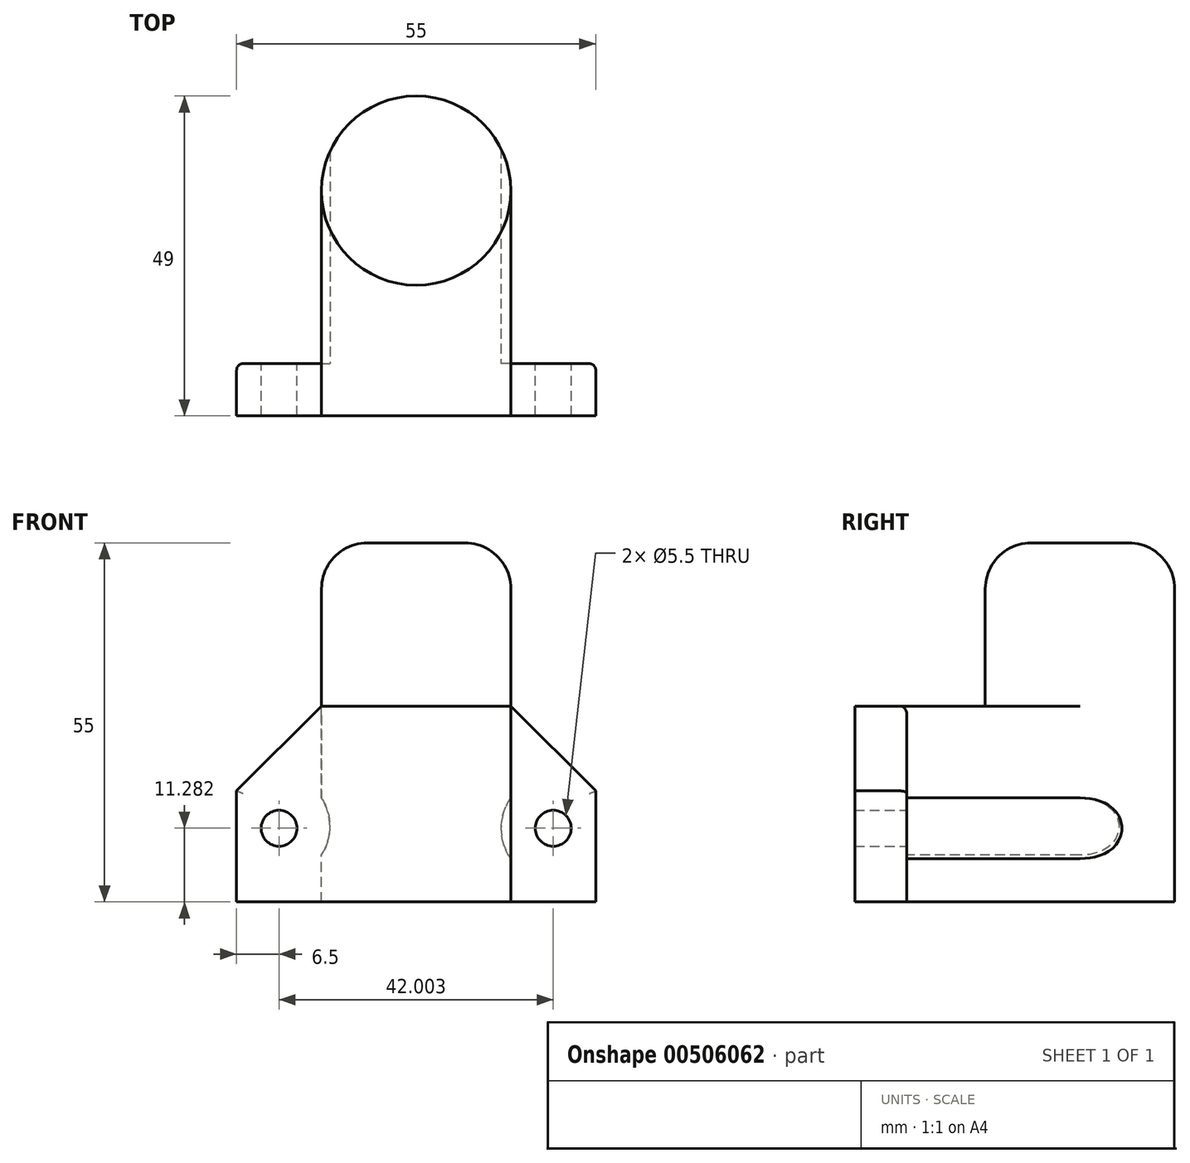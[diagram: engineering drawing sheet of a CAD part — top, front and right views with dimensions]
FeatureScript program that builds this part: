
annotation { "Feature Type Name" : "Feature", "Feature Type Description" : "" }
export const myFeature = defineFeature(function(context is Context, id is Id, definition is map)
    precondition{}
    {
        {
            var Q0;
            Q0=qCreatedBy(makeId("Right.planeOp"),FACE);
            var sketch = newSketch(context, id + "F0", { "sketchPlane" : qUnion([Q0])});
            skLineSegment(sketch, "E0.bottom", {"start": v(0, 0) * mm, "end": v(49, 0) * mm});
            skLineSegment(sketch, "E0.top", {"start": v(0, 30) * mm, "end": v(49, 30) * mm});
            skLineSegment(sketch, "E0.left", {"start": v(0, 0) * mm, "end": v(0, 30) * mm});
            skLineSegment(sketch, "E0.right", {"start": v(49, 0) * mm, "end": v(49, 30) * mm});
            skSolve(sketch);
        }
        {
            var Q0;
            Q0 = qSketchRegion(id + "F0", true);
            extrude(context, id + "F1", {"entities" : qUnion([Q0]), "depth" : 29 * mm});
        }
        {
            var Q0;
            Q0=qCreatedBy(makeId("Front.planeOp"),FACE);
            var sketch = newSketch(context, id + "F2", { "sketchPlane" : qUnion([Q0])});
            skLineSegment(sketch, "E1", {"start": v(0, 0) * mm, "end": v(-13, 0) * mm});
            skLineSegment(sketch, "E2", {"start": v(-13, 0) * mm, "end": v(-13, 17) * mm});
            skLineSegment(sketch, "E3", {"start": v(-13, 17) * mm, "end": v(0, 30) * mm});
            skLineSegment(sketch, "E4", {"start": v(0, 30) * mm, "end": v(0, 0) * mm});
            skLineSegment(sketch, "E5", {"start": v(0, 0) * mm, "end": v(29, 0) * mm});
            skLineSegment(sketch, "E6.MirrorCS", {"start": v(42, 0) * mm, "end": v(42, 17) * mm});
            skLineSegment(sketch, "E7.MirrorCS", {"start": v(42, 17) * mm, "end": v(29, 30) * mm});
            skLineSegment(sketch, "E8.MirrorCS", {"start": v(29, 0) * mm, "end": v(42, 0) * mm});
            skLineSegment(sketch, "E9.MirrorCS", {"start": v(29, 30) * mm, "end": v(29, 0) * mm});
            skSolve(sketch);
        }
        {
            var Q0;
            Q0 = qSketchRegion(id + "F2", true);
            extrude(context, id + "F3", {"entities" : qUnion([Q0]), "operationType" : NewBodyOperationType.ADD, "oppositeDirection" : true, "depth" : 8 * mm});
        }
        {
            var Q0;
            Q0=makeQuery(id+"F1.opExtrude","SWEPT_FACE",FACE,{"disambiguationData":[OSD([sQuery(id+"F0.wireOp",EDGE,"E0.top")])]});
            var sketch = newSketch(context, id + "F4", { "sketchPlane" : qUnion([Q0])});
            skLineSegment(sketch, "E10", {"start": v(14.5, 49) * mm, "end": v(14.5, 0) * mm});
            skPoint(sketch, "E11", {"position": v(14.5, 34.5) * mm});
            skCircle(sketch, "E12", {"center": v(14.5, 34.5) * mm, "radius": 14.5 * mm});
            skSolve(sketch);
        }
        {
            var Q0;
            Q0 = qSketchRegion(id + "F4", true);
            extrude(context, id + "F5", {"entities" : qUnion([Q0]), "operationType" : NewBodyOperationType.ADD, "depth" : 25 * mm});
        }
        {
            var Q0;
            {var subQ0=sQuery(id+"F0.wireOp",EDGE,"E0.right");var subQ1=sQuery(id+"F0.wireOp",EDGE,"E0.top");var subQ2=makeQuery(id+"F1.opExtrude","SWEPT_FACE",FACE,{"disambiguationData":[OSD([subQ1])]});Q0=makeQuery(id+"F5.boolean.opBoolean","SPLIT",FACE,{"disambiguationData":[TD([makeQuery(id+"F1.opExtrude","CAP_FACE",FACE,{"disambiguationData":[OSD([sQuery(id+"F0.wireOp",EDGE,"E0.bottom"),subQ1,sQuery(id+"F0.wireOp",EDGE,"E0.left"),subQ0])],"isStart":false}),subQ2,makeQuery(id+"F1.opExtrude","SWEPT_FACE",FACE,{"disambiguationData":[OSD([subQ0])]}),makeQuery(id+"F5.opExtrude","SWEPT_FACE",FACE,{"disambiguationData":[OSD([sQuery(id+"F4.wireOp",EDGE,"E12")])]})])],"derivedFrom":subQ2});}
            var Q1;
            {var subQ0=sQuery(id+"F0.wireOp",EDGE,"E0.right");var subQ1=sQuery(id+"F0.wireOp",EDGE,"E0.top");var subQ2=makeQuery(id+"F1.opExtrude","SWEPT_FACE",FACE,{"disambiguationData":[OSD([subQ1])]});Q1=makeQuery(id+"F5.boolean.opBoolean","SPLIT",FACE,{"disambiguationData":[TD([makeQuery(id+"F1.opExtrude","CAP_FACE",FACE,{"disambiguationData":[OSD([sQuery(id+"F0.wireOp",EDGE,"E0.bottom"),subQ1,sQuery(id+"F0.wireOp",EDGE,"E0.left"),subQ0])],"isStart":true}),subQ2,makeQuery(id+"F1.opExtrude","SWEPT_FACE",FACE,{"disambiguationData":[OSD([subQ0])]}),makeQuery(id+"F5.opExtrude","SWEPT_FACE",FACE,{"disambiguationData":[OSD([sQuery(id+"F4.wireOp",EDGE,"E12")])]})])],"derivedFrom":subQ2});}
            extrude(context, id + "F6", {"entities" : qUnion([Q0, Q1]), "operationType" : NewBodyOperationType.REMOVE, "oppositeDirection" : true, "depth" : 30 * mm});
        }
        {
            var Q0;
            Q0=makeQuery(id+"F5.opExtrude","CAP_FACE",FACE,{"disambiguationData":[OSD([sQuery(id+"F4.wireOp",EDGE,"E12")])],"isStart":false});
            fillet(context, id + "F7", {"entities" : qUnion([Q0]), "radius" : 7 * mm, "tangentPropagation" : true, "allowEdgeOverflow" : false});
        }
        {
            var Q0;
            Q0=makeQuery(id+"F3.opExtrude","CAP_FACE",FACE,{"disambiguationData":[OSD([sQuery(id+"F2.wireOp",EDGE,"E6.MirrorCS"),sQuery(id+"F2.wireOp",EDGE,"E7.MirrorCS"),sQuery(id+"F2.wireOp",EDGE,"E8.MirrorCS"),sQuery(id+"F2.wireOp",EDGE,"E9.MirrorCS")])],"isStart":false});
            var sketch = newSketch(context, id + "F8", { "sketchPlane" : qUnion([Q0])});
            skCircle(sketch, "E13", {"center": v(-35.5, 11.28) * mm, "radius": 2.75 * mm});
            skCircle(sketch, "E14", {"center": v(6.5, 11.28) * mm, "radius": 2.75 * mm});
            skSolve(sketch);
        }
        {
            var Q0;
            Q0 = qSketchRegion(id + "F8", true);
            extrude(context, id + "F9", {"entities" : qUnion([Q0]), "operationType" : NewBodyOperationType.REMOVE, "oppositeDirection" : true, "depth" : 25 * mm});
        }
        {
            var Q0;
            Q0=makeQuery(id+"F3.opExtrude","CAP_FACE",FACE,{"disambiguationData":[OSD([sQuery(id+"F2.wireOp",EDGE,"E6.MirrorCS"),sQuery(id+"F2.wireOp",EDGE,"E7.MirrorCS"),sQuery(id+"F2.wireOp",EDGE,"E8.MirrorCS"),sQuery(id+"F2.wireOp",EDGE,"E9.MirrorCS")])],"isStart":false});
            var sketch = newSketch(context, id + "F10", { "sketchPlane" : qUnion([Q0])});
            skCircle(sketch, "E15", {"center": v(-35.5, 11.28) * mm, "radius": 8 * mm});
            skLineSegment(sketch, "E16", {"start": v(-14.5, 30) * mm, "end": v(-14.4, 10.9) * mm});
            skCircle(sketch, "E17.MirrorC", {"center": v(6.7, 11.52) * mm, "radius": 8 * mm});
            skSolve(sketch);
        }
        {
            var Q0;
            Q0 = qSketchRegion(id + "F10", true);
            extrude(context, id + "F11", {"entities" : qUnion([Q0]), "operationType" : NewBodyOperationType.REMOVE, "depth" : 40 * mm});
        }
        {
            var Q0;
            Q0=makeQuery(id+"F3.opExtrude","CAP_EDGE",EDGE,{"disambiguationData":[OSD([sQuery(id+"F2.wireOp",EDGE,"E7.MirrorCS")])],"isStart":false});
            var Q1;
            Q1=makeQuery(id+"F3.opExtrude","CAP_EDGE",EDGE,{"disambiguationData":[OSD([sQuery(id+"F2.wireOp",EDGE,"E6.MirrorCS")])],"isStart":false});
            var Q2;
            Q2=makeQuery(id+"F3.opExtrude","CAP_EDGE",EDGE,{"disambiguationData":[OSD([sQuery(id+"F2.wireOp",EDGE,"E3")])],"isStart":false});
            var Q3;
            Q3=makeQuery(id+"F3.opExtrude","CAP_EDGE",EDGE,{"disambiguationData":[OSD([sQuery(id+"F2.wireOp",EDGE,"E2")])],"isStart":false});
            fillet(context, id + "F12", {"entities" : qUnion([Q0, Q1, Q2, Q3]), "radius" : 1 * mm, "tangentPropagation" : true, "allowEdgeOverflow" : false});
        }
    });
